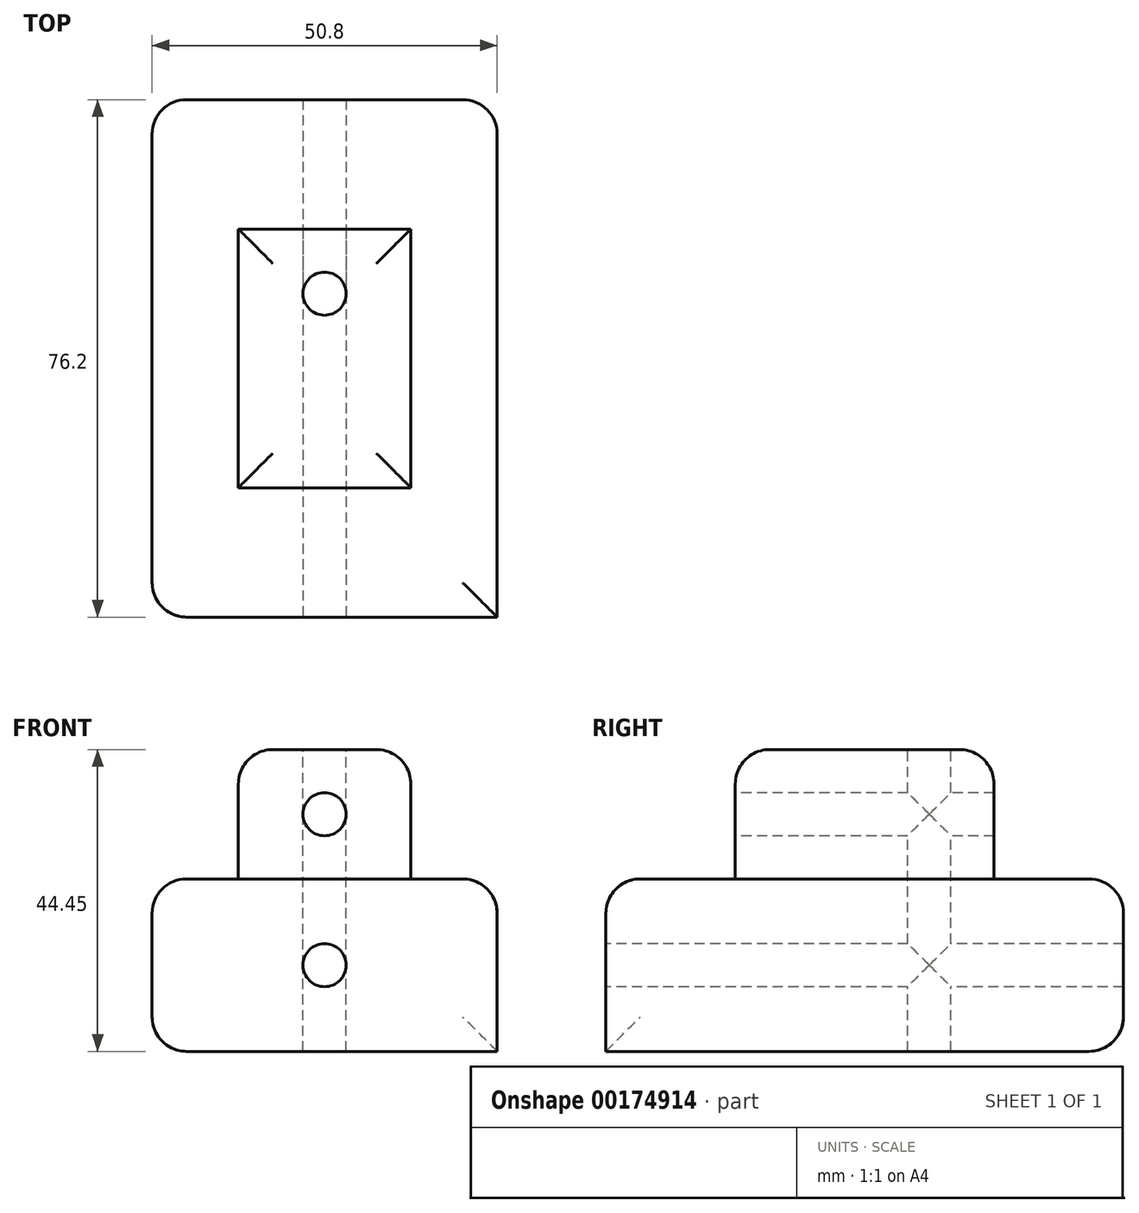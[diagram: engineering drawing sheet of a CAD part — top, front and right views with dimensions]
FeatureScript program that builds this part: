
annotation { "Feature Type Name" : "Feature", "Feature Type Description" : "" }
export const myFeature = defineFeature(function(context is Context, id is Id, definition is map)
    precondition{}
    {
        {
            var Q0;
            Q0=qCreatedBy(makeId("Front.planeOp"),FACE);
            var sketch = newSketch(context, id + "F0", { "sketchPlane" : qUnion([Q0])});
            skLineSegment(sketch, "E0.bottom", {"start": v(0, 0) * mm, "end": v(-50.8, 0) * mm});
            skLineSegment(sketch, "E0.top", {"start": v(0, 25.4) * mm, "end": v(-50.8, 25.4) * mm});
            skLineSegment(sketch, "E0.left", {"start": v(0, 0) * mm, "end": v(0, 25.4) * mm});
            skLineSegment(sketch, "E0.right", {"start": v(-50.8, 0) * mm, "end": v(-50.8, 25.4) * mm});
            skSolve(sketch);
        }
        {
            var Q0;
            Q0 = qSketchRegion(id + "F0", true);
            extrude(context, id + "F1", {"entities" : qUnion([Q0]), "depth" : 76.2 * mm});
        }
        {
            var Q0;
            Q0=makeQuery(id+"F1.opExtrude","SWEPT_FACE",FACE,{"disambiguationData":[OSD([sQuery(id+"F0.wireOp",EDGE,"E0.top")])]});
            var sketch = newSketch(context, id + "F2", { "sketchPlane" : qUnion([Q0])});
            skLineSegment(sketch, "E1.bottom", {"start": v(-38.1, -19.05) * mm, "end": v(-12.7, -19.05) * mm});
            skLineSegment(sketch, "E1.top", {"start": v(-38.1, -57.15) * mm, "end": v(-12.7, -57.15) * mm});
            skLineSegment(sketch, "E1.left", {"start": v(-38.1, -19.05) * mm, "end": v(-38.1, -57.15) * mm});
            skLineSegment(sketch, "E1.right", {"start": v(-12.7, -19.05) * mm, "end": v(-12.7, -57.15) * mm});
            skSolve(sketch);
        }
        {
            var Q0;
            Q0 = qSketchRegion(id + "F2", true);
            extrude(context, id + "F3", {"entities" : qUnion([Q0]), "operationType" : NewBodyOperationType.ADD, "depth" : 19.05 * mm});
        }
        {
            var Q0;
            Q0=makeQuery(id+"F3.opExtrude","CAP_FACE",FACE,{"disambiguationData":[OSD([sQuery(id+"F2.wireOp",EDGE,"E1.bottom"),sQuery(id+"F2.wireOp",EDGE,"E1.top"),sQuery(id+"F2.wireOp",EDGE,"E1.left"),sQuery(id+"F2.wireOp",EDGE,"E1.right")])],"isStart":false});
            var sketch = newSketch(context, id + "F4", { "sketchPlane" : qUnion([Q0])});
            skCircle(sketch, "E2", {"center": v(-25.4, -28.58) * mm, "radius": 3.18 * mm});
            skSolve(sketch);
        }
        {
            var Q0;
            Q0=makeQuery(id+"F4.imprint","IMPRINT",FACE,{"disambiguationData":[TD([[makeQuery(id+"F4.imprint","IMPRINT",EDGE,{"derivedFrom":sQuery(id+"F4.wireOp",EDGE,"E2")}),1.0]])]});
            extrude(context, id + "F5", {"entities" : qUnion([Q0]), "operationType" : NewBodyOperationType.REMOVE, "oppositeDirection" : true, "depth" : 44.45 * mm});
        }
        {
            var Q0;
            Q0=makeQuery(id+"F1.opExtrude","CAP_FACE",FACE,{"disambiguationData":[OSD([sQuery(id+"F0.wireOp",EDGE,"E0.bottom"),sQuery(id+"F0.wireOp",EDGE,"E0.top"),sQuery(id+"F0.wireOp",EDGE,"E0.left"),sQuery(id+"F0.wireOp",EDGE,"E0.right")])],"isStart":false});
            var sketch = newSketch(context, id + "F6", { "sketchPlane" : qUnion([Q0])});
            skCircle(sketch, "E3", {"center": v(-25.4, 12.7) * mm, "radius": 3.18 * mm});
            skSolve(sketch);
        }
        {
            var Q0;
            Q0=makeQuery(id+"F6.imprint","IMPRINT",FACE,{"disambiguationData":[TD([[makeQuery(id+"F6.imprint","IMPRINT",EDGE,{"derivedFrom":sQuery(id+"F6.wireOp",EDGE,"E3")}),1.0]])]});
            extrude(context, id + "F7", {"entities" : qUnion([Q0]), "operationType" : NewBodyOperationType.REMOVE, "oppositeDirection" : true, "depth" : 76.2 * mm});
        }
        {
            var Q0;
            Q0=makeQuery(id+"F3.opExtrude","SWEPT_FACE",FACE,{"disambiguationData":[OSD([sQuery(id+"F2.wireOp",EDGE,"E1.top")])]});
            var sketch = newSketch(context, id + "F8", { "sketchPlane" : qUnion([Q0])});
            skCircle(sketch, "E4", {"center": v(-25.4, 34.93) * mm, "radius": 3.18 * mm});
            skSolve(sketch);
        }
        {
            var Q0;
            Q0 = qSketchRegion(id + "F8", true);
            extrude(context, id + "F9", {"entities" : qUnion([Q0]), "operationType" : NewBodyOperationType.REMOVE, "oppositeDirection" : true, "depth" : 38.1 * mm});
        }
        {
            var Q0;
            Q0=makeQuery(id+"F3.opExtrude","CAP_EDGE",EDGE,{"disambiguationData":[OSD([sQuery(id+"F2.wireOp",EDGE,"E1.left")])],"isStart":false});
            var Q1;
            Q1=makeQuery(id+"F3.opExtrude","CAP_EDGE",EDGE,{"disambiguationData":[OSD([sQuery(id+"F2.wireOp",EDGE,"E1.bottom")])],"isStart":false});
            var Q2;
            Q2=makeQuery(id+"F3.opExtrude","CAP_EDGE",EDGE,{"disambiguationData":[OSD([sQuery(id+"F2.wireOp",EDGE,"E1.right")])],"isStart":false});
            var Q3;
            Q3=makeQuery(id+"F3.opExtrude","CAP_EDGE",EDGE,{"disambiguationData":[OSD([sQuery(id+"F2.wireOp",EDGE,"E1.top")])],"isStart":false});
            var Q4;
            Q4=makeQuery(id+"F3.opExtrude","CAP_EDGE",EDGE,{"disambiguationData":[OSD([sQuery(id+"F2.wireOp",EDGE,"E1.bottom")])],"isStart":true});
            var Q5;
            Q5=makeQuery(id+"F3.opExtrude","CAP_EDGE",EDGE,{"disambiguationData":[OSD([sQuery(id+"F2.wireOp",EDGE,"E1.left")])],"isStart":true});
            var Q6;
            Q6=makeQuery(id+"F1.opExtrude","CAP_EDGE",EDGE,{"disambiguationData":[OSD([sQuery(id+"F0.wireOp",EDGE,"E0.top")])],"isStart":true});
            var Q7;
            Q7=makeQuery(id+"F1.opExtrude","CAP_EDGE",EDGE,{"disambiguationData":[OSD([sQuery(id+"F0.wireOp",EDGE,"E0.left")])],"isStart":true});
            var Q8;
            Q8=makeQuery(id+"F1.opExtrude","CAP_EDGE",EDGE,{"disambiguationData":[OSD([sQuery(id+"F0.wireOp",EDGE,"E0.bottom")])],"isStart":true});
            var Q9;
            Q9=makeQuery(id+"F1.opExtrude","CAP_EDGE",EDGE,{"disambiguationData":[OSD([sQuery(id+"F0.wireOp",EDGE,"E0.right")])],"isStart":true});
            var Q10;
            Q10=makeQuery(id+"F1.opExtrude","SWEPT_EDGE",EDGE,{"disambiguationData":[OSD([sQuery(id+"F0.wireOp",EDGE,"E0.top"),sQuery(id+"F0.wireOp",EDGE,"E0.right")])]});
            var Q11;
            Q11=makeQuery(id+"F1.opExtrude","SWEPT_EDGE",EDGE,{"disambiguationData":[OSD([sQuery(id+"F0.wireOp",EDGE,"E0.bottom"),sQuery(id+"F0.wireOp",EDGE,"E0.right")])]});
            var Q12;
            Q12=makeQuery(id+"F1.opExtrude","CAP_EDGE",EDGE,{"disambiguationData":[OSD([sQuery(id+"F0.wireOp",EDGE,"E0.right")])],"isStart":false});
            var Q13;
            Q13=makeQuery(id+"F1.opExtrude","CAP_EDGE",EDGE,{"disambiguationData":[OSD([sQuery(id+"F0.wireOp",EDGE,"E0.top")])],"isStart":false});
            var Q14;
            Q14=makeQuery(id+"F1.opExtrude","SWEPT_EDGE",EDGE,{"disambiguationData":[OSD([sQuery(id+"F0.wireOp",EDGE,"E0.top"),sQuery(id+"F0.wireOp",EDGE,"E0.left")])]});
            fillet(context, id + "F10", {"entities" : qUnion([Q0, Q1, Q2, Q3, Q4, Q5, Q6, Q7, Q8, Q9, Q10, Q11, Q12, Q13, Q14]), "radius" : 5.08 * mm, "tangentPropagation" : true, "allowEdgeOverflow" : false});
        }
    });
